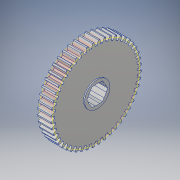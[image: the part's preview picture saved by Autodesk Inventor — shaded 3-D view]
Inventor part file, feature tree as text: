
AUTODESK INVENTOR PART (.ipt)
format: ipt  version: 2018 (Build 220112000, 112)  size: 333,312 bytes
history: native  units: in
note: dims shown in document units (in); Inventor stores cm internally (conversion verified against a paired STEP export)
features: other x3, sketch x1
ambient origin geometry x8: Origin, YZ Plane, XZ Plane, XY Plane, X Axis, Y Axis, Z Axis, Center Point
bodies: Solid1 (feature_tree)
feature tree (4):
  sketch  "Sketch1"  dims[d0=2.4in d1=1.0in d2=0.0in]
  other  "Srf1"
  other  "Cut-Extrude3"
  other  "pitch circle"
